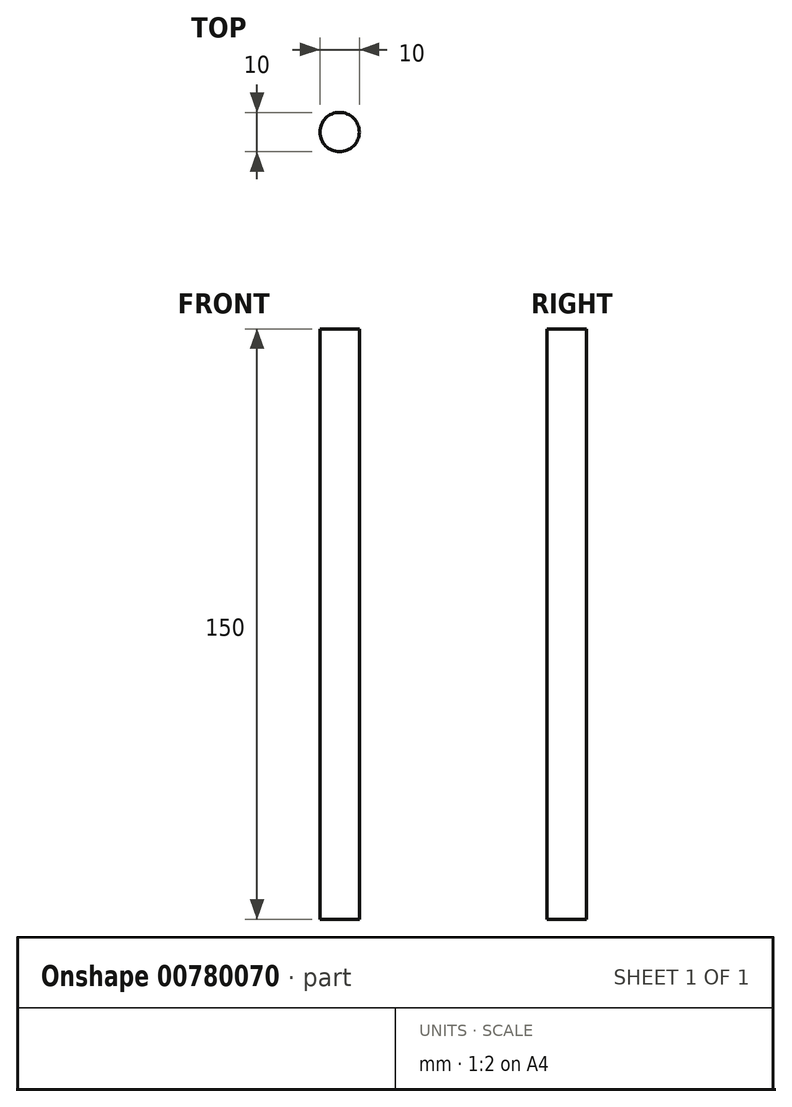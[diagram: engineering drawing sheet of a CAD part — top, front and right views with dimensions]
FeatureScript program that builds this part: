
annotation { "Feature Type Name" : "Feature", "Feature Type Description" : "" }
export const myFeature = defineFeature(function(context is Context, id is Id, definition is map)
    precondition{}
    {
        {
            var Q0;
            Q0=qCreatedBy(makeId("Top.planeOp"),FACE);
            var sketch = newSketch(context, id + "F0", { "sketchPlane" : qUnion([Q0])});
            skCircle(sketch, "E0", {"center": v(0, 0) * mm, "radius": 5 * mm});
            skSolve(sketch);
        }
        {
            var Q0;
            Q0=makeQuery(id+"F0.imprint","IMPRINT",FACE,{"disambiguationData":[TD([[makeQuery(id+"F0.imprint","IMPRINT",EDGE,{"derivedFrom":sQuery(id+"F0.wireOp",EDGE,"E0")}),1.0]])]});
            extrude(context, id + "F1", {"entities" : qUnion([Q0]), "depth" : 150 * mm, "offsetDistance" : 25 * mm});
        }
    });
